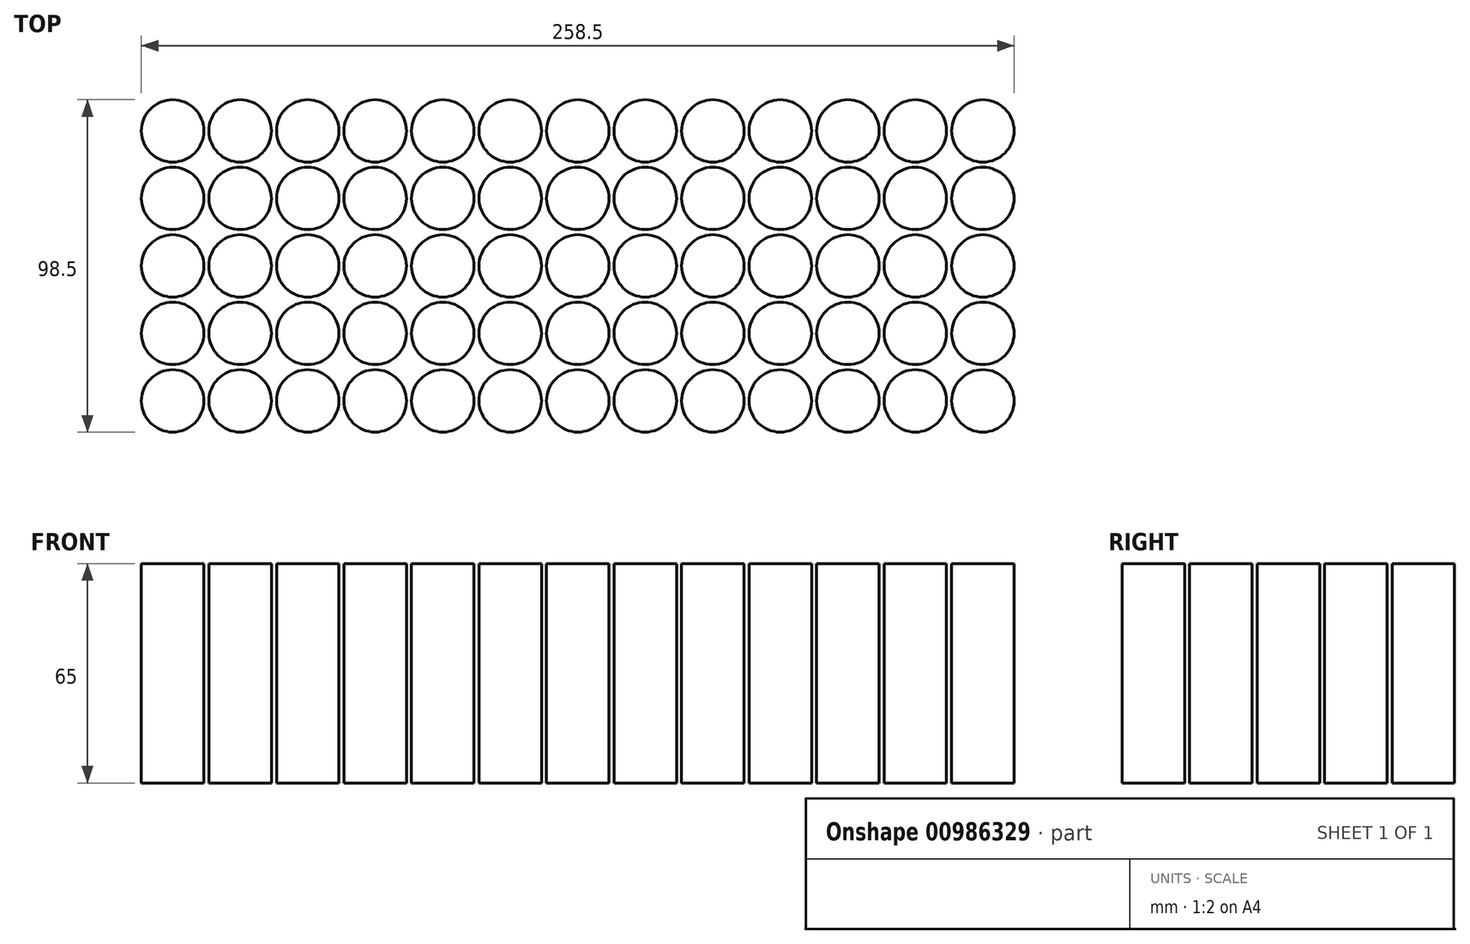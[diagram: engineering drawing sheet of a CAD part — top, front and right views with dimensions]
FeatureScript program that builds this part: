
annotation { "Feature Type Name" : "Feature", "Feature Type Description" : "" }
export const myFeature = defineFeature(function(context is Context, id is Id, definition is map)
    precondition{}
    {
        {
            var Q0;
            Q0=qCreatedBy(makeId("Top.planeOp"),FACE);
            var sketch = newSketch(context, id + "F0", { "sketchPlane" : qUnion([Q0])});
            skCircle(sketch, "E0", {"center": v(-84, 22.79) * mm, "radius": 9.25 * mm});
            skCircle(sketch, "E1.0.1.0", {"center": v(-84, 42.79) * mm, "radius": 9.25 * mm});
            skCircle(sketch, "E1.0.2.0", {"center": v(-84, 62.79) * mm, "radius": 9.25 * mm});
            skCircle(sketch, "E1.0.3.0", {"center": v(-84, 82.79) * mm, "radius": 9.25 * mm});
            skCircle(sketch, "E1.0.4.0", {"center": v(-84, 102.79) * mm, "radius": 9.25 * mm});
            skCircle(sketch, "E1.1.0.0", {"center": v(-64, 22.79) * mm, "radius": 9.25 * mm});
            skCircle(sketch, "E1.1.1.0", {"center": v(-64, 42.79) * mm, "radius": 9.25 * mm});
            skCircle(sketch, "E1.1.2.0", {"center": v(-64, 62.79) * mm, "radius": 9.25 * mm});
            skCircle(sketch, "E1.1.3.0", {"center": v(-64, 82.79) * mm, "radius": 9.25 * mm});
            skCircle(sketch, "E1.1.4.0", {"center": v(-64, 102.79) * mm, "radius": 9.25 * mm});
            skCircle(sketch, "E1.2.0.0", {"center": v(-44, 22.79) * mm, "radius": 9.25 * mm});
            skCircle(sketch, "E1.2.1.0", {"center": v(-44, 42.79) * mm, "radius": 9.25 * mm});
            skCircle(sketch, "E1.2.2.0", {"center": v(-44, 62.79) * mm, "radius": 9.25 * mm});
            skCircle(sketch, "E1.2.3.0", {"center": v(-44, 82.79) * mm, "radius": 9.25 * mm});
            skCircle(sketch, "E1.2.4.0", {"center": v(-44, 102.79) * mm, "radius": 9.25 * mm});
            skCircle(sketch, "E1.3.0.0", {"center": v(-24, 22.79) * mm, "radius": 9.25 * mm});
            skCircle(sketch, "E1.3.1.0", {"center": v(-24, 42.79) * mm, "radius": 9.25 * mm});
            skCircle(sketch, "E1.3.2.0", {"center": v(-24, 62.79) * mm, "radius": 9.25 * mm});
            skCircle(sketch, "E1.3.3.0", {"center": v(-24, 82.79) * mm, "radius": 9.25 * mm});
            skCircle(sketch, "E1.3.4.0", {"center": v(-24, 102.79) * mm, "radius": 9.25 * mm});
            skCircle(sketch, "E1.4.0.0", {"center": v(-4, 22.79) * mm, "radius": 9.25 * mm});
            skCircle(sketch, "E1.4.1.0", {"center": v(-4, 42.79) * mm, "radius": 9.25 * mm});
            skCircle(sketch, "E1.4.2.0", {"center": v(-4, 62.79) * mm, "radius": 9.25 * mm});
            skCircle(sketch, "E1.4.3.0", {"center": v(-4, 82.79) * mm, "radius": 9.25 * mm});
            skCircle(sketch, "E1.4.4.0", {"center": v(-4, 102.79) * mm, "radius": 9.25 * mm});
            skCircle(sketch, "E1.5.0.0", {"center": v(16, 22.79) * mm, "radius": 9.25 * mm});
            skCircle(sketch, "E1.5.1.0", {"center": v(16, 42.79) * mm, "radius": 9.25 * mm});
            skCircle(sketch, "E1.5.2.0", {"center": v(16, 62.79) * mm, "radius": 9.25 * mm});
            skCircle(sketch, "E1.5.3.0", {"center": v(16, 82.79) * mm, "radius": 9.25 * mm});
            skCircle(sketch, "E1.5.4.0", {"center": v(16, 102.79) * mm, "radius": 9.25 * mm});
            skCircle(sketch, "E1.6.0.0", {"center": v(36, 22.79) * mm, "radius": 9.25 * mm});
            skCircle(sketch, "E1.6.1.0", {"center": v(36, 42.79) * mm, "radius": 9.25 * mm});
            skCircle(sketch, "E1.6.2.0", {"center": v(36, 62.79) * mm, "radius": 9.25 * mm});
            skCircle(sketch, "E1.6.3.0", {"center": v(36, 82.79) * mm, "radius": 9.25 * mm});
            skCircle(sketch, "E1.6.4.0", {"center": v(36, 102.79) * mm, "radius": 9.25 * mm});
            skCircle(sketch, "E1.7.0.0", {"center": v(56, 22.79) * mm, "radius": 9.25 * mm});
            skCircle(sketch, "E1.7.1.0", {"center": v(56, 42.79) * mm, "radius": 9.25 * mm});
            skCircle(sketch, "E1.7.2.0", {"center": v(56, 62.79) * mm, "radius": 9.25 * mm});
            skCircle(sketch, "E1.7.3.0", {"center": v(56, 82.79) * mm, "radius": 9.25 * mm});
            skCircle(sketch, "E1.7.4.0", {"center": v(56, 102.79) * mm, "radius": 9.25 * mm});
            skCircle(sketch, "E1.8.0.0", {"center": v(76, 22.79) * mm, "radius": 9.25 * mm});
            skCircle(sketch, "E1.8.1.0", {"center": v(76, 42.79) * mm, "radius": 9.25 * mm});
            skCircle(sketch, "E1.8.2.0", {"center": v(76, 62.79) * mm, "radius": 9.25 * mm});
            skCircle(sketch, "E1.8.3.0", {"center": v(76, 82.79) * mm, "radius": 9.25 * mm});
            skCircle(sketch, "E1.8.4.0", {"center": v(76, 102.79) * mm, "radius": 9.25 * mm});
            skCircle(sketch, "E1.9.0.0", {"center": v(96, 22.79) * mm, "radius": 9.25 * mm});
            skCircle(sketch, "E1.9.1.0", {"center": v(96, 42.79) * mm, "radius": 9.25 * mm});
            skCircle(sketch, "E1.9.2.0", {"center": v(96, 62.79) * mm, "radius": 9.25 * mm});
            skCircle(sketch, "E1.9.3.0", {"center": v(96, 82.79) * mm, "radius": 9.25 * mm});
            skCircle(sketch, "E1.9.4.0", {"center": v(96, 102.79) * mm, "radius": 9.25 * mm});
            skCircle(sketch, "E1.10.0.0", {"center": v(116, 22.79) * mm, "radius": 9.25 * mm});
            skCircle(sketch, "E1.10.1.0", {"center": v(116, 42.79) * mm, "radius": 9.25 * mm});
            skCircle(sketch, "E1.10.2.0", {"center": v(116, 62.79) * mm, "radius": 9.25 * mm});
            skCircle(sketch, "E1.10.3.0", {"center": v(116, 82.79) * mm, "radius": 9.25 * mm});
            skCircle(sketch, "E1.10.4.0", {"center": v(116, 102.79) * mm, "radius": 9.25 * mm});
            skCircle(sketch, "E1.11.0.0", {"center": v(136, 22.79) * mm, "radius": 9.25 * mm});
            skCircle(sketch, "E1.11.1.0", {"center": v(136, 42.79) * mm, "radius": 9.25 * mm});
            skCircle(sketch, "E1.11.2.0", {"center": v(136, 62.79) * mm, "radius": 9.25 * mm});
            skCircle(sketch, "E1.11.3.0", {"center": v(136, 82.79) * mm, "radius": 9.25 * mm});
            skCircle(sketch, "E1.11.4.0", {"center": v(136, 102.79) * mm, "radius": 9.25 * mm});
            skCircle(sketch, "E1.12.0.0", {"center": v(156, 22.79) * mm, "radius": 9.25 * mm});
            skCircle(sketch, "E1.12.1.0", {"center": v(156, 42.79) * mm, "radius": 9.25 * mm});
            skCircle(sketch, "E1.12.2.0", {"center": v(156, 62.79) * mm, "radius": 9.25 * mm});
            skCircle(sketch, "E1.12.3.0", {"center": v(156, 82.79) * mm, "radius": 9.25 * mm});
            skCircle(sketch, "E1.12.4.0", {"center": v(156, 102.79) * mm, "radius": 9.25 * mm});
            skLineSegment(sketch, "E1.direction1", {"start": v(-84, 22.79) * mm, "end": v(-64, 22.79) * mm, "construction": true});
            skLineSegment(sketch, "E1.direction2", {"start": v(-84, 22.79) * mm, "end": v(-84, 42.79) * mm, "construction": true});
            skSolve(sketch);
        }
        {
            var Q0;
            Q0 = qSketchRegion(id + "F0", true);
            extrude(context, id + "F1", {"entities" : qUnion([Q0]), "depth" : 65 * mm, "offsetDistance" : 25 * mm});
        }
    });
